# Revit family: Bath-Alcove-Kohler-Mariposa-K-1259-AW
name_source: partatom
category: Plumbing Fixtures
revit_build: Autodesk Revit 2015 (Build: 20140606_1530(x64)
units: mm (PartAtom-declared; Revit-internal decimal feet)

## types (10) — shared parameters
ADA Compliant = No
Apparent Load = 120 VA
Assembly Code = D2010510
CW Connection = No
Default Elevation = 0' - 0"
Drain Diameter = 0' - 1 1/2"
Electrical Connector = 120V, 15A
Electrical Note = Provide one grounded electrical outlet within 24'' (610 mm) of each component
HW Connection = No
Height = 1' - 9 1/4"
Keynote = 22 40 00.D2
Length = 6' - 0"
Manufacturer = Kohler
Material = Acrylic
Number of Poles = 1
Product Documentation Link = http://www.us.kohler.com
Product Name = Mariposa 72'' x 36'' Alcove Bath with Bask and Apron
Product Page URL = http://www.us.kohler.com
Sanitary Connector = Sanitary Drain
URL = http://www.us.kohler.com
Vent Connection = Yes
Version = 2014 - v1.0a
Voltage = 120 V
Waste Connection = Yes
Water Capacity = 72 gal (272.5 L)
Weight = 77 lbs (34.9 kg)
Width = 3' - 0"
zero-valued in all types: CWFU, HWFU, Power Factor, WFU

## per-type parameters (varying)
| type | Constraint | ControlM | Description | Finish | Model |
| Right Drain Apron, 0-White | 1 | 1425 | 72'' x 36'' Alcove Bath, Right Hand Drain with Bask, Flange and Apron, Dune | Acrylic - Kohler - NY - Dune | K-1259-RAW-NY |
| Right Drain Apron, 47-Almond | 1 | 47 | 72'' x 36'' Alcove Bath, Right Hand Drain with Bask, Flange and Apron, Almond | Acrylic - Kohler - 47 - Almond | K-1259-RAW-47 |
| Right Drain Apron, 96-Biscut | 1 | 96 | 72'' x 36'' Alcove Bath, Right Hand Drain with Bask, Flange and Apron, Biscuit | Acrylic - Kohler - 96 - Biscuit | K-1259-RAW-96 |
| Right Drain Apron, G9-Sandbar | 1 | 79 | 72'' x 36'' Alcove Bath, Right Hand Drain with Bask, Flange and Apron, Sandbar | Acrylic - Kohler - G9 - Sandbar | K-1259-RAW-G9 |
| Right Drain Apron, NY-Dune | 1 | 1425 | 72'' x 36'' Alcove Bath, Right Hand Drain with Bask, Flange and Apron, Dune | Acrylic - Kohler - NY - Dune | K-1259-RAW-NY |
| Left Drain Apron, 0-White | 2 | 0 | 72'' x 36'' Alcove Bath, Left Hand Drain with Bask, Flange and Apron, White | Acrylic - Kohler - 0 - White | K-1259-LAW-0 |
| Left Drain Apron, 47-Almond | 2 | 47 | 72'' x 36'' Alcove Bath, Left Hand Drain with Bask, Flange and Apron, Almond | Acrylic - Kohler - 47 - Almond | K-1259-LAW-47 |
| Left Drain Apron, 96-Biscut | 2 | 96 | 72'' x 36'' Alcove Bath, Left Hand Drain with Bask, Flange and Apron, Biscuit | Acrylic - Kohler - 96 - Biscuit | K-1259-LAW-96 |
| Left Drain Apron, G9-Sandbar | 2 | 79 | 72'' x 36'' Alcove Bath, Left Hand Drain with Bask, Flange and Apron, Sandbar | Acrylic - Kohler - G9 - Sandbar | K-1259-LAW-G9 |
| Left Drain Apron, NY-Dune | 2 | 1425 | 72'' x 36'' Alcove Bath, Left Hand Drain with Bask, Flange and Apron, Dune | Acrylic - Kohler - NY - Dune | K-1259-LAW-NY |

## geometry (parser evidence)
native form markers: Extrusion x6, Sweep x7
no freeform markers — native parametric forms only
